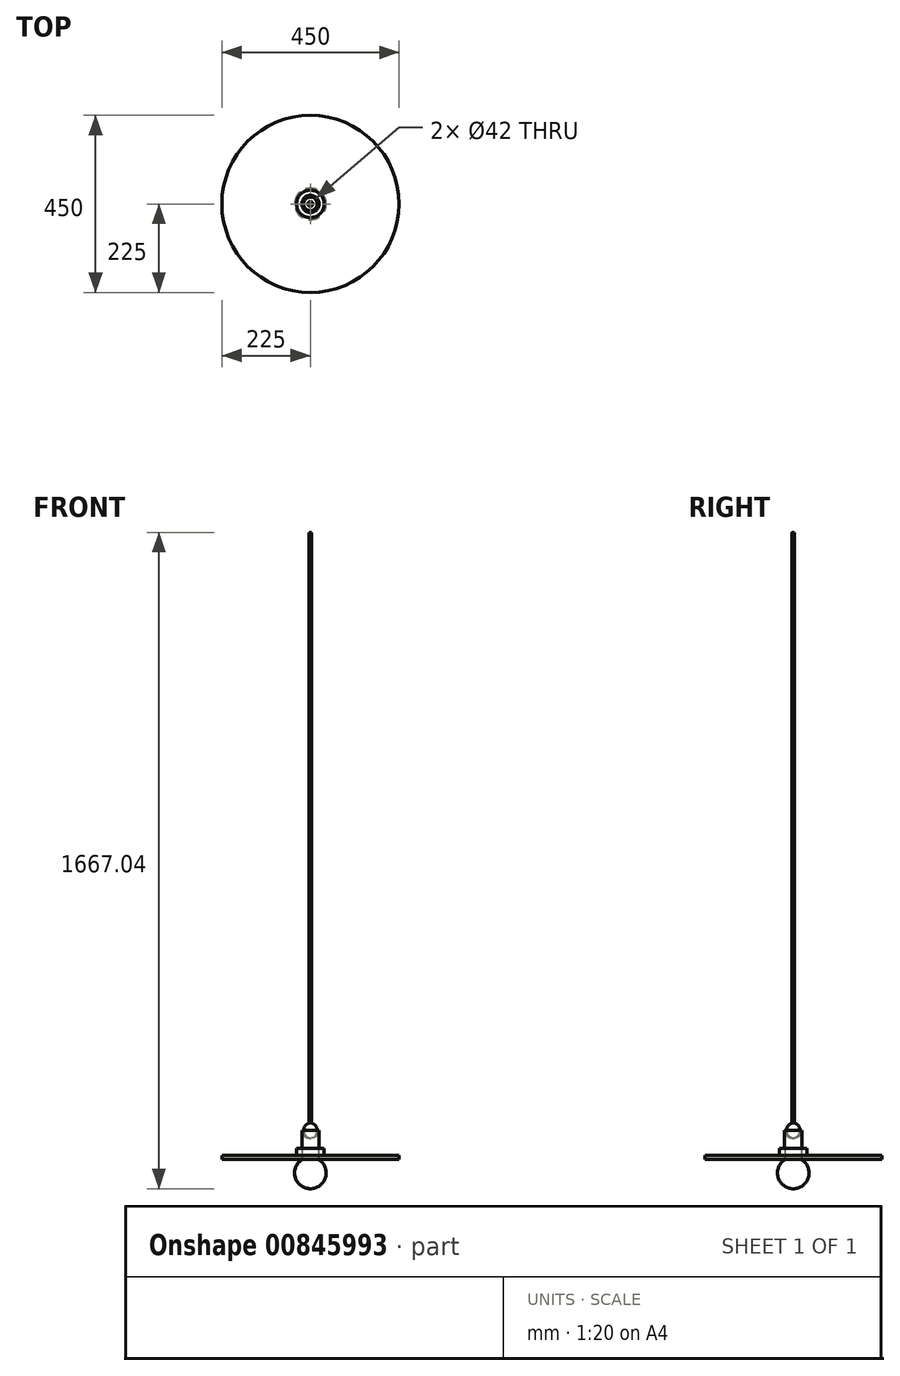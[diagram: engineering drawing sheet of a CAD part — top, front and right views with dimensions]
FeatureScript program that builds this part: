
annotation { "Feature Type Name" : "Feature", "Feature Type Description" : "" }
export const myFeature = defineFeature(function(context is Context, id is Id, definition is map)
    precondition{}
    {
        {
            var Q0;
            Q0=qCreatedBy(makeId("Top.planeOp"),FACE);
            var sketch = newSketch(context, id + "F0", { "sketchPlane" : qUnion([Q0])});
            skCircle(sketch, "E0", {"center": v(0, 0) * mm, "radius": 225 * mm});
            skCircle(sketch, "E1", {"center": v(0, 0) * mm, "radius": 21 * mm});
            skSolve(sketch);
        }
        {
            var Q0;
            Q0=qSketchRegion(id+"F0",true);
            extrude(context, id + "F1", {"entities" : qUnion([Q0]), "depth" : 10 * mm, "offsetDistance" : 25.4 * mm});
        }
        {
            var Q0;
            Q0=makeQuery(id+"F1.opExtrude","CAP_FACE",FACE,{"disambiguationData":[OSD([sQuery(id+"F0.wireOp",EDGE,"E0"),sQuery(id+"F0.wireOp",EDGE,"E1")])],"isStart":false});
            var sketch = newSketch(context, id + "F2", { "sketchPlane" : qUnion([Q0])});
            skCircle(sketch, "E2", {"center": v(0, 0) * mm, "radius": 21 * mm});
            skCircle(sketch, "E3", {"center": v(0, 0) * mm, "radius": 35 * mm});
            skSolve(sketch);
        }
        {
            var Q0;
            Q0=qSketchRegion(id+"F2",true);
            extrude(context, id + "F3", {"entities" : qUnion([Q0]), "depth" : 18 * mm, "offsetDistance" : 25 * mm});
        }
        {
            var Q0;
            Q0=qCreatedBy(makeId("Front.planeOp"),FACE);
            var sketch = newSketch(context, id + "F4", { "sketchPlane" : qUnion([Q0])});
            skLineSegment(sketch, "E4", {"start": v(0, 28) * mm, "end": v(0, 93) * mm});
            skLineSegment(sketch, "E5", {"start": v(0, 93) * mm, "end": v(-6.32, 93) * mm});
            skLineSegment(sketch, "E6", {"start": v(0, 28) * mm, "end": v(-21.82, 28) * mm});
            skLineSegment(sketch, "E7", {"start": v(-21.82, 28) * mm, "end": v(-21.82, 73.9) * mm});
            skArc(sketch, "E8", {"start": v(-6.32, 93) * mm, "mid": v(-17.45, 86.2) * mm, "end": v(-21.82, 73.9) * mm});
            skSolve(sketch);
        }
        {
            var Q0;
            Q0=qSketchRegion(id+"F4",true);
            var Q1;
            Q1=sQuery(id+"F4.wireOp",EDGE,"E4");
            revolve(context, id + "F5", {"surfaceOperationType" : NewSurfaceOperationType.NEW, "entities" : qUnion([Q0]), "axis" : qUnion([Q1]), "revolveType" : RevolveType.FULL});
        }
        {
            var Q0;
            Q0=qCreatedBy(makeId("Front.planeOp"),FACE);
            var sketch = newSketch(context, id + "F6", { "sketchPlane" : qUnion([Q0])});
            skArc(sketch, "E9", {"start": v(-21, 0) * mm, "mid": v(-38.48, -44.96) * mm, "end": v(0, -74.04) * mm});
            skLineSegment(sketch, "E10", {"start": v(0, 0) * mm, "end": v(-21, 0) * mm});
            skLineSegment(sketch, "E11", {"start": v(0, 0) * mm, "end": v(0, -74.04) * mm});
            skSolve(sketch);
        }
        {
            var Q0;
            Q0=qSketchRegion(id+"F6",true);
            var Q1;
            Q1=sQuery(id+"F6.wireOp",EDGE,"E11");
            revolve(context, id + "F7", {"surfaceOperationType" : NewSurfaceOperationType.NEW, "entities" : qUnion([Q0]), "axis" : qUnion([Q1]), "revolveType" : RevolveType.FULL});
        }
        {
            var Q0;
            Q0=makeQuery(id+"F5.opRevolve","SWEPT_FACE",FACE,{"disambiguationData":[OSD([sQuery(id+"F4.wireOp",EDGE,"E5")])]});
            var sketch = newSketch(context, id + "F8", { "sketchPlane" : qUnion([Q0])});
            skCircle(sketch, "E12", {"center": v(0, 0) * mm, "radius": 3 * mm});
            skSolve(sketch);
        }
        {
            var Q0;
            Q0=qSketchRegion(id+"F8",true);
            extrude(context, id + "F9", {"entities" : qUnion([Q0]), "depth" : 1500 * mm, "offsetDistance" : 25 * mm});
        }
    });
